# Revit family: Glulam-Western Species-Column
name_source: partatom
category: Structural Columns
revit_build: Autodesk Revit Architecture 2012 (Build: 20110210_1515)
units: mm (PartAtom-declared; Revit-internal decimal feet)

## types (164) — shared parameters
Assembly Code = B10

## per-type parameters (varying)
| type | A | Ix | Iy | Laminations | Sx | Sy | b | d |
| 2.5x6 | 15 in² | 45 | 7.81 | 4 | 15 | 6.25 | 0' - 2 1/2" | 0' - 6" |
| 2.5x7.5 | 18.75 in² | 87.89 | 9.77 | 5 | 23.44 | 7.81 | 0' - 2 1/2" | 0' - 7 1/2" |
| 2.5x9 | 22.5 in² | 151.9 | 11.72 | 6 | 33.75 | 9.38 | 0' - 2 1/2" | 0' - 9" |
| 2.5x10.5 | 26.25 in² | 241.2 | 13.67 | 7 | 45.94 | 10.94 | 0' - 2 1/2" | 0' - 10 1/2" |
| 2.5x12 | 30 in² | 360 | 15.63 | 8 | 60 | 12.5 | 0' - 2 1/2" | 1' - 0" |
| 2.5x13.5 | 33.75 in² | 512.6 | 17.58 | 9 | 75.94 | 14.06 | 0' - 2 1/2" | 1' - 1 1/2" |
| 2.5x15 | 37.5 in² | 703.1 | 19.53 | 10 | 93.75 | 15.63 | 0' - 2 1/2" | 1' - 3" |
| 2.5x16.5 | 41.25 in² | 935.9 | 21.48 | 11 | 113.4 | 17.19 | 0' - 2 1/2" | 1' - 4 1/2" |
| 2.5x18 | 45 in² | 1215 | 23.44 | 12 | 135 | 18.75 | 0' - 2 1/2" | 1' - 6" |
| 2.5x19.5 | 48.75 in² | 1545 | 25.39 | 13 | 158.4 | 20.31 | 0' - 2 1/2" | 1' - 7 1/2" |
| 2.5x21 | 52.5 in² | 1929 | 27.34 | 14 | 183.8 | 21.88 | 0' - 2 1/2" | 1' - 9" |
| 2.5x22.5 | 56.25 in² | 2373 | 29.3 | 15 | 210.9 | 23.44 | 0' - 2 1/2" | 1' - 10 1/2" |
| 2.5x24 | 60 in² | 2880 | 31.25 | 16 | 240 | 25 | 0' - 2 1/2" | 2' - 0" |
| 2.5x25.5 | 63.75 in² | 3454 | 33.2 | 17 | 270.9 | 26.56 | 0' - 2 1/2" | 2' - 1 1/2" |
| 2.5x27 | 67.5 in² | 4101 | 35.16 | 18 | 303.8 | 28.13 | 0' - 2 1/2" | 2' - 3" |
| 3.125x6 | 18.75 in² | 56.25 | 15.26 | 4 | 18.75 | 9.77 | 0' - 3 1/8" | 0' - 6" |
| 3.125x7.5 | 23.44 in² | 109.9 | 19.07 | 5 | 29.3 | 12.21 | 0' - 3 1/8" | 0' - 7 1/2" |
| 3.125x9 | 28.13 in² | 189.8 | 22.9 | 6 | 42.19 | 14.65 | 0' - 3 1/8" | 0' - 9" |
| 3.125x10.5 | 32.81 in² | 301.5 | 26.7 | 7 | 57.42 | 17.09 | 0' - 3 1/8" | 0' - 10 1/2" |
| 3.125x12 | 37.5 in² | 450 | 30.52 | 8 | 75 | 19.53 | 0' - 3 1/8" | 1' - 0" |
| 3.125x13.5 | 42.19 in² | 640.7 | 34.33 | 9 | 94.92 | 21.97 | 0' - 3 1/8" | 1' - 1 1/2" |
| 3.125x15 | 46.88 in² | 878.9 | 38.15 | 10 | 117.2 | 24.41 | 0' - 3 1/8" | 1' - 3" |
| 3.125x16.5 | 51.56 in² | 1170 | 41.96 | 11 | 141.8 | 26.86 | 0' - 3 1/8" | 1' - 4 1/2" |
| 3.125x18 | 56.25 in² | 1519 | 45.78 | 12 | 168.8 | 29.3 | 0' - 3 1/8" | 1' - 6" |
| 3.125x19.5 | 60.94 in² | 1931 | 49.59 | 13 | 198 | 31.74 | 0' - 3 1/8" | 1' - 7 1/2" |
| 3.125x21 | 65.63 in² | 2412 | 53.41 | 14 | 229.7 | 34.18 | 0' - 3 1/8" | 1' - 9" |
| 3.125x22.5 | 70.31 in² | 2966 | 57.22 | 15 | 263.7 | 36.62 | 0' - 3 1/8" | 1' - 10 1/2" |
| 3.125x24 | 75 in² | 3600 | 61.04 | 16 | 300 | 39.06 | 0' - 3 1/8" | 2' - 0" |
| 3.125x25.5 | 79.69 in² | 4318 | 64.85 | 17 | 338.7 | 41.5 | 0' - 3 1/8" | 2' - 1 1/2" |
| 3.125x27 | 84.38 in² | 5126 | 68.66 | 18 | 379.7 | 43.95 | 0' - 3 1/8" | 2' - 3" |
| 5.125x6 | 30.75 in² | 92.3 | 67.31 | 4 | 30.75 | 26.27 | 0' - 5 1/8" | 0' - 6" |
| 5.125x7.5 | 38.44 in² | 180.2 | 84.13 | 5 | 48.05 | 32.83 | 0' - 5 1/8" | 0' - 7 1/2" |
| 5.125x9 | 46.13 in² | 311.3 | 101 | 6 | 69.19 | 39.4 | 0' - 5 1/8" | 0' - 9" |
| 5.125x10.5 | 53.81 in² | 494.4 | 117.8 | 7 | 94.17 | 45.96 | 0' - 5 1/8" | 0' - 10 1/2" |
| 5.125x12 | 61.5 in² | 738 | 134.6 | 8 | 123 | 52.53 | 0' - 5 1/8" | 1' - 0" |
| 5.125x13.5 | 69.19 in² | 1051 | 151.4 | 9 | 155.7 | 59.1 | 0' - 5 1/8" | 1' - 1 1/2" |
| 5.125x15 | 76.88 in² | 1441 | 168.3 | 10 | 192.2 | 65.66 | 0' - 5 1/8" | 1' - 3" |
| 5.125x16.5 | 84.56 in² | 1919 | 185.1 | 11 | 232.5 | 72.23 | 0' - 5 1/8" | 1' - 4 1/2" |
| 5.125x18 | 92.25 in² | 2491 | 201.9 | 12 | 276.8 | 78.8 | 0' - 5 1/8" | 1' - 6" |
| 5.125x19.5 | 99.94 in² | 3167 | 218.7 | 13 | 324.8 | 85.36 | 0' - 5 1/8" | 1' - 7 1/2" |
| 5.125x21 | 107.6 in² | 3955 | 235.6 | 14 | 376.7 | 91.93 | 0' - 5 1/8" | 1' - 9" |
| 5.125x22.5 | 115.3 in² | 4865 | 252.4 | 15 | 432.4 | 98.5 | 0' - 5 1/8" | 1' - 10 1/2" |
| 5.125x24 | 123 in² | 5904 | 269.2 | 16 | 492 | 105.1 | 0' - 5 1/8" | 2' - 0" |
| 5.125x25.5 | 130.7 in² | 7082 | 286 | 17 | 555.4 | 111.6 | 0' - 5 1/8" | 2' - 1 1/2" |
| 5.125x27 | 138.4 in² | 8406 | 302.9 | 18 | 622.7 | 118.2 | 0' - 5 1/8" | 2' - 3" |
| 5.125x28.5 | 146.1 in² | 9887 | 319.7 | 19 | 693.8 | 124.8 | 0' - 5 1/8" | 2' - 4 1/2" |
| 5.125x30 | 153.8 in² | 11531 | 336.5 | 20 | 768.8 | 131.3 | 0' - 5 1/8" | 2' - 6" |
| 5.125x31.5 | 161.4 in² | 13349 | 353.4 | 21 | 847.5 | 137.9 | 0' - 5 1/8" | 2' - 7 1/2" |
| 5.125x33 | 169.1 in² | 15348 | 370.2 | 22 | 930.2 | 144.5 | 0' - 5 1/8" | 2' - 9" |
| 5.125x34.5 | 176.8 in² | 17538 | 387 | 23 | 1017 | 151 | 0' - 5 1/8" | 2' - 10 1/2" |
| 5.125x36 | 184.5 in² | 19926 | 403.8 | 24 | 1107 | 157.6 | 0' - 5 1/8" | 3' - 0" |
| 6.75x7.5 | 50.63 in² | 237.3 | 192.2 | 5 | 63.28 | 56.95 | 0' - 6 3/4" | 0' - 7 1/2" |
| 6.75x9 | 60.75 in² | 410.1 | 230.7 | 6 | 91.13 | 68.34 | 0' - 6 3/4" | 0' - 9" |
| 6.75x10.5 | 70.88 in² | 651.2 | 269.1 | 7 | 124 | 79.73 | 0' - 6 3/4" | 0' - 10 1/2" |
| 6.75x12 | 81 in² | 972 | 307.5 | 8 | 162 | 91.13 | 0' - 6 3/4" | 1' - 0" |
| 6.75x13.5 | 91.13 in² | 1384 | 346 | 9 | 205 | 102.5 | 0' - 6 3/4" | 1' - 1 1/2" |
| 6.75x15 | 101.3 in² | 1898 | 384.4 | 10 | 253.1 | 113.9 | 0' - 6 3/4" | 1' - 3" |
| 6.75x16.5 | 111.4 in² | 2527 | 422.9 | 11 | 306.3 | 125.3 | 0' - 6 3/4" | 1' - 4 1/2" |
| 6.75x18 | 121.5 in² | 3281 | 461.3 | 12 | 364.5 | 136.7 | 0' - 6 3/4" | 1' - 6" |
| 6.75x19.5 | 131.6 in² | 4171 | 499.8 | 13 | 427.8 | 148.1 | 0' - 6 3/4" | 1' - 7 1/2" |
| 6.75x21 | 141.8 in² | 5209 | 538.2 | 14 | 496.1 | 159.5 | 0' - 6 3/4" | 1' - 9" |
| 6.75x22.5 | 151.9 in² | 6407 | 576.7 | 15 | 569.5 | 170.9 | 0' - 6 3/4" | 1' - 10 1/2" |
| 6.75x24 | 162 in² | 7776 | 615.1 | 16 | 648 | 182.3 | 0' - 6 3/4" | 2' - 0" |
| 6.75x25.5 | 172.1 in² | 9327 | 653.5 | 17 | 731.5 | 193.6 | 0' - 6 3/4" | 2' - 1 1/2" |
| 6.75x27 | 182.3 in² | 11072 | 692 | 18 | 820.1 | 205 | 0' - 6 3/4" | 2' - 3" |
| 6.75x28.5 | 192.4 in² | 13021 | 730.4 | 19 | 913.8 | 216.4 | 0' - 6 3/4" | 2' - 4 1/2" |
| 6.75x30 | 202.5 in² | 15188 | 768.9 | 20 | 1013 | 227.8 | 0' - 6 3/4" | 2' - 6" |
| 6.75x31.5 | 212.6 in² | 17581 | 807.3 | 21 | 1116 | 239.2 | 0' - 6 3/4" | 2' - 7 1/2" |
| 6.75x33 | 222.8 in² | 20215 | 845.8 | 22 | 1225 | 250.6 | 0' - 6 3/4" | 2' - 9" |
| 6.75x34.5 | 232.9 in² | 23098 | 884.2 | 23 | 1339 | 262 | 0' - 6 3/4" | 2' - 10 1/2" |
| 6.75x36 | 243 in² | 26244 | 922.6 | 24 | 1458 | 273.4 | 0' - 6 3/4" | 3' - 0" |
| 6.75x37.5 | 253.1 in² | 29663 | 961.1 | 25 | 1582 | 284.8 | 0' - 6 3/4" | 3' - 1 1/2" |
| 6.75x39 | 263.3 in² | 33367 | 999.5 | 26 | 1711 | 296.2 | 0' - 6 3/4" | 3' - 3" |
| 6.75x40.5 | 273.4 in² | 37367 | 1038 | 27 | 1845 | 307.5 | 0' - 6 3/4" | 3' - 4 1/2" |
| 6.75x42 | 283.5 in² | 41675 | 1076 | 28 | 1985 | 318.9 | 0' - 6 3/4" | 3' - 6" |
| 6.75x43.5 | 293.6 in² | 46301 | 1115 | 29 | 2129 | 330.3 | 0' - 6 3/4" | 3' - 7 1/2" |
| 6.75x45 | 303.8 in² | 51258 | 1153 | 30 | 2278 | 341.7 | 0' - 6 3/4" | 3' - 9" |
| 6.75x46.5 | 313.9 in² | 56556 | 1192 | 31 | 2433 | 353.1 | 0' - 6 3/4" | 3' - 10 1/2" |
| 6.75x48 | 324 in² | 62208 | 1230 | 32 | 2592 | 364.5 | 0' - 6 3/4" | 4' - 0" |
| 8.75x9 | 78.8 in² | 531.6 | 502.4 | 6 | 118.1 | 114.8 | 0' - 8 3/4" | 0' - 9" |
| 8.75x10.5 | 91.9 in² | 844.1 | 586.2 | 7 | 160.8 | 134 | 0' - 8 3/4" | 0' - 10 1/2" |
| 8.75x12 | 105 in² | 1260 | 669.9 | 8 | 210 | 153.1 | 0' - 8 3/4" | 1' - 0" |
| 8.75x13.5 | 118.1 in² | 1794 | 753.7 | 9 | 265.8 | 172.3 | 0' - 8 3/4" | 1' - 1 1/2" |
| 8.75x15 | 131.3 in² | 2461 | 837.4 | 10 | 328.1 | 191.4 | 0' - 8 3/4" | 1' - 3" |
| 8.75x16.5 | 144.4 in² | 3276 | 921.1 | 11 | 397 | 210.5 | 0' - 8 3/4" | 1' - 4 1/2" |
| 8.75x18 | 157.5 in² | 4253 | 1005 | 12 | 472.5 | 229.7 | 0' - 8 3/4" | 1' - 6" |
| 8.75x19.5 | 170.6 in² | 5407 | 1089 | 13 | 554.5 | 248.8 | 0' - 8 3/4" | 1' - 7 1/2" |
| 8.75x21 | 183.8 in² | 6753 | 1172 | 14 | 643.1 | 268 | 0' - 8 3/4" | 1' - 9" |
| 8.75x22.5 | 196.9 in² | 8306 | 1256 | 15 | 738.3 | 287.1 | 0' - 8 3/4" | 1' - 10 1/2" |
| 8.75x24 | 210 in² | 10080 | 1340 | 16 | 840 | 306.3 | 0' - 8 3/4" | 2' - 0" |
| 8.75x25.5 | 223.1 in² | 12091 | 1424 | 17 | 948.3 | 325.4 | 0' - 8 3/4" | 2' - 1 1/2" |
| 8.75x27 | 236.3 in² | 14352 | 1507 | 18 | 1063 | 344.5 | 0' - 8 3/4" | 2' - 3" |
| 8.75x28.5 | 249.4 in² | 16880 | 1591 | 19 | 1185 | 363.7 | 0' - 8 3/4" | 2' - 4 1/2" |
| 8.75x30 | 262.5 in² | 19688 | 1675 | 20 | 1313 | 382.8 | 0' - 8 3/4" | 2' - 6" |
| 8.75x31.5 | 275.6 in² | 22791 | 1759 | 21 | 1447 | 402 | 0' - 8 3/4" | 2' - 7 1/2" |
| 8.75x33 | 288.8 in² | 26204 | 1842 | 22 | 1588 | 421.1 | 0' - 8 3/4" | 2' - 9" |
| 8.75x34.5 | 301.9 in² | 29942 | 1926 | 23 | 1736 | 440.2 | 0' - 8 3/4" | 2' - 10 1/2" |
| 8.75x36 | 315 in² | 34020 | 2010 | 24 | 1890 | 459.4 | 0' - 8 3/4" | 3' - 0" |
| 8.75x37.5 | 328.1 in² | 38452 | 2094 | 25 | 2051 | 478.5 | 0' - 8 3/4" | 3' - 1 1/2" |
| 8.75x39 | 341.3 in² | 43253 | 2177 | 26 | 2218 | 497.7 | 0' - 8 3/4" | 3' - 3" |
| 8.75x40.5 | 354.4 in² | 48439 | 2261 | 27 | 2392 | 516.8 | 0' - 8 3/4" | 3' - 4 1/2" |
| 8.75x42 | 367.5 in² | 54023 | 2345 | 28 | 2573 | 535.9 | 0' - 8 3/4" | 3' - 6" |
| 8.75x43.5 | 380.6 in² | 60020 | 2428 | 29 | 2760 | 555.1 | 0' - 8 3/4" | 3' - 7 1/2" |
| 8.75x45 | 393.8 in² | 66445 | 2512 | 30 | 2953 | 574.2 | 0' - 8 3/4" | 3' - 9" |
| 8.75x46.5 | 406.9 in² | 73314 | 2596 | 31 | 3153 | 593.4 | 0' - 8 3/4" | 3' - 10 1/2" |
| 8.75x48 | 420 in² | 80640 | 2680 | 32 | 3360 | 612.5 | 0' - 8 3/4" | 4' - 0" |
| 8.75x49.5 | 433.1 in² | 88439 | 2763 | 33 | 3573 | 631.6 | 0' - 8 3/4" | 4' - 1 1/2" |
| 8.75x51 | 446.3 in² | 96725 | 2847 | 34 | 3793 | 650.8 | 0' - 8 3/4" | 4' - 3" |
| 8.75x52.5 | 459.4 in² | 105513 | 2931 | 35 | 4020 | 669.9 | 0' - 8 3/4" | 4' - 4 1/2" |
| 8.75x54 | 472.5 in² | 114818 | 3015 | 36 | 4253 | 689.1 | 0' - 8 3/4" | 4' - 6" |
| 8.75x55.5 | 485.6 in² | 124654 | 3098 | 37 | 4492 | 708.2 | 0' - 8 3/4" | 4' - 7 1/2" |
| 8.75x57 | 498.8 in² | 135037 | 3182 | 38 | 4738 | 727.3 | 0' - 8 3/4" | 4' - 9" |
| 8.75x58.5 | 511.9 in² | 145980 | 3266 | 39 | 4991 | 746.5 | 0' - 8 3/4" | 4' - 10 1/2" |
| 8.75x60 | 525 in² | 157500 | 3350 | 40 | 5250 | 765.6 | 0' - 8 3/4" | 5' - 0" |
| 8.75x61.5 | 538.1 in² | 169610 | 3433 | 41 | 5516 | 784.8 | 0' - 8 3/4" | 5' - 1 1/2" |
| 8.75x63 | 551.3 in² | 182326 | 3517 | 42 | 5788 | 803.9 | 0' - 8 3/4" | 5' - 3" |
| 10.75x10.5 | 112.9 in² | 1037 | 1087 | 7 | 197.5 | 202.2 | 0' - 10 3/4" | 0' - 10 1/2" |
| 10.75x12 | 129 in² | 1548 | 1242 | 8 | 258 | 231.1 | 0' - 10 3/4" | 1' - 0" |
| 10.75x13.5 | 145.1 in² | 2204 | 1398 | 9 | 326.5 | 260 | 0' - 10 3/4" | 1' - 1 1/2" |
| 10.75x15 | 161.3 in² | 3023 | 1553 | 10 | 403.1 | 288.9 | 0' - 10 3/4" | 1' - 3" |
| 10.75x16.5 | 177.4 in² | 4024 | 1708 | 11 | 487.8 | 317.8 | 0' - 10 3/4" | 1' - 4 1/2" |
| 10.75x18 | 193.5 in² | 5225 | 1863 | 12 | 580.5 | 346.7 | 0' - 10 3/4" | 1' - 6" |
| 10.75x19.5 | 209.6 in² | 6642 | 2019 | 13 | 681.3 | 375.6 | 0' - 10 3/4" | 1' - 7 1/2" |
| 10.75x21 | 225.8 in² | 8296 | 2174 | 14 | 790.1 | 404.5 | 0' - 10 3/4" | 1' - 9" |
| 10.75x22.5 | 241.9 in² | 10204 | 2329 | 15 | 907 | 433.4 | 0' - 10 3/4" | 1' - 10 1/2" |
| 10.75x24 | 258 in² | 12384 | 2485 | 16 | 1032 | 462.3 | 0' - 10 3/4" | 2' - 0" |
| 10.75x25.5 | 274.1 in² | 14854 | 2640 | 17 | 1165 | 491.1 | 0' - 10 3/4" | 2' - 1 1/2" |
| 10.75x27 | 290.3 in² | 17633 | 2795 | 18 | 1306 | 520 | 0' - 10 3/4" | 2' - 3" |
| 10.75x28.5 | 306.4 in² | 20738 | 2950 | 19 | 1455 | 548.9 | 0' - 10 3/4" | 2' - 4 1/2" |
| 10.75x30 | 322.5 in² | 24188 | 3106 | 20 | 1613 | 577.8 | 0' - 10 3/4" | 2' - 6" |
| 10.75x31.5 | 338.6 in² | 28000 | 3261 | 21 | 1778 | 606.7 | 0' - 10 3/4" | 2' - 7 1/2" |
| 10.75x33 | 354.8 in² | 32194 | 3416 | 22 | 1951 | 635.6 | 0' - 10 3/4" | 2' - 9" |
| 10.75x34.5 | 370.9 in² | 36786 | 3572 | 23 | 2133 | 664.5 | 0' - 10 3/4" | 2' - 10 1/2" |
| 10.75x36 | 387 in² | 41796 | 3727 | 24 | 2322 | 693.4 | 0' - 10 3/4" | 3' - 0" |
| 10.75x37.5 | 403.1 in² | 47241 | 3882 | 25 | 2520 | 722.3 | 0' - 10 3/4" | 3' - 1 1/2" |
| 10.75x39 | 419.3 in² | 53140 | 4037 | 26 | 2725 | 751.2 | 0' - 10 3/4" | 3' - 3" |
| 10.75x40.5 | 435.4 in² | 59510 | 4193 | 27 | 2939 | 780 | 0' - 10 3/4" | 3' - 4 1/2" |
| 10.75x42 | 451.5 in² | 66371 | 4348 | 28 | 3161 | 808.9 | 0' - 10 3/4" | 3' - 6" |
| 10.75x43.5 | 467.6 in² | 73739 | 4503 | 29 | 3390 | 837.8 | 0' - 10 3/4" | 3' - 7 1/2" |
| 10.75x45 | 483.8 in² | 81633 | 4659 | 30 | 3628 | 866.7 | 0' - 10 3/4" | 3' - 9" |
| 10.75x46.5 | 499.9 in² | 90071 | 4814 | 31 | 3874 | 895.6 | 0' - 10 3/4" | 3' - 10 1/2" |
| 10.75x48 | 516 in² | 99072 | 4969 | 32 | 4128 | 924.5 | 0' - 10 3/4" | 4' - 0" |
| 10.75x49.5 | 532.1 in² | 108653 | 5124 | 33 | 4390 | 953.4 | 0' - 10 3/4" | 4' - 1 1/2" |
| 10.75x51 | 548.3 in² | 118833 | 5280 | 34 | 4660 | 982.3 | 0' - 10 3/4" | 4' - 3" |
| 10.75x52.5 | 564.4 in² | 129630 | 5435 | 35 | 4938 | 1011 | 0' - 10 3/4" | 4' - 4 1/2" |
| 10.75x54 | 580.5 in² | 141062 | 5590 | 36 | 5225 | 1040 | 0' - 10 3/4" | 4' - 6" |
| 10.75x55.5 | 596.6 in² | 153146 | 5746 | 37 | 5519 | 1069 | 0' - 10 3/4" | 4' - 7 1/2" |
| 10.75x57 | 612.8 in² | 165902 | 5901 | 38 | 5821 | 1098 | 0' - 10 3/4" | 4' - 9" |
| 10.75x58.5 | 628.9 in² | 179347 | 6056 | 39 | 6132 | 1127 | 0' - 10 3/4" | 4' - 10 1/2" |
| 10.75x60 | 645 in² | 193500 | 6211 | 40 | 6450 | 1156 | 0' - 10 3/4" | 5' - 0" |
| 10.75x61.5 | 661.1 in² | 208378 | 6367 | 41 | 6777 | 1185 | 0' - 10 3/4" | 5' - 1 1/2" |
| 10.75x63 | 677.3 in² | 224000 | 6522 | 42 | 7111 | 1213 | 0' - 10 3/4" | 5' - 3" |
| 10.75x64.5 | 693.4 in² | 240384 | 6677 | 43 | 7454 | 1242 | 0' - 10 3/4" | 5' - 4 1/2" |
| 10.75x66 | 709.5 in² | 257549 | 6833 | 44 | 7805 | 1271 | 0' - 10 3/4" | 5' - 6" |
| 10.75x67.5 | 725.6 in² | 275511 | 6988 | 45 | 8163 | 1300 | 0' - 10 3/4" | 5' - 7 1/2" |
| 10.75x69 | 741.8 in² | 294289 | 7143 | 46 | 8530 | 1329 | 0' - 10 3/4" | 5' - 9" |
| 10.75x70.5 | 757.9 in² | 313902 | 7298 | 47 | 8905 | 1358 | 0' - 10 3/4" | 5' - 10 1/2" |
| 10.75x72 | 774 in² | 334368 | 7454 | 48 | 9288 | 1387 | 0' - 10 3/4" | 6' - 0" |
| 10.75x73.5 | 790.1 in² | 355704 | 7609 | 49 | 9679 | 1416 | 0' - 10 3/4" | 6' - 1 1/2" |
| 10.75x75 | 806.3 in² | 377930 | 7764 | 50 | 10078 | 1445 | 0' - 10 3/4" | 6' - 3" |
| 10.75x76.5 | 822.4 in² | 401062 | 7920 | 51 | 10485 | 1473 | 0' - 10 3/4" | 6' - 4 1/2" |
| 10.75x78 | 838.5 in² | 425120 | 8075 | 52 | 10901 | 1502 | 0' - 10 3/4" | 6' - 6" |
| 10.75x79.5 | 854.6 in² | 450120 | 8230 | 53 | 11324 | 1531 | 0' - 10 3/4" | 6' - 7 1/2" |
| 10.75x81 | 870.8 in² | 476083 | 8386 | 54 | 11755 | 1560 | 0' - 10 3/4" | 6' - 9" |

## geometry (parser evidence)
native form markers: Sweep x1
no freeform markers — native parametric forms only
